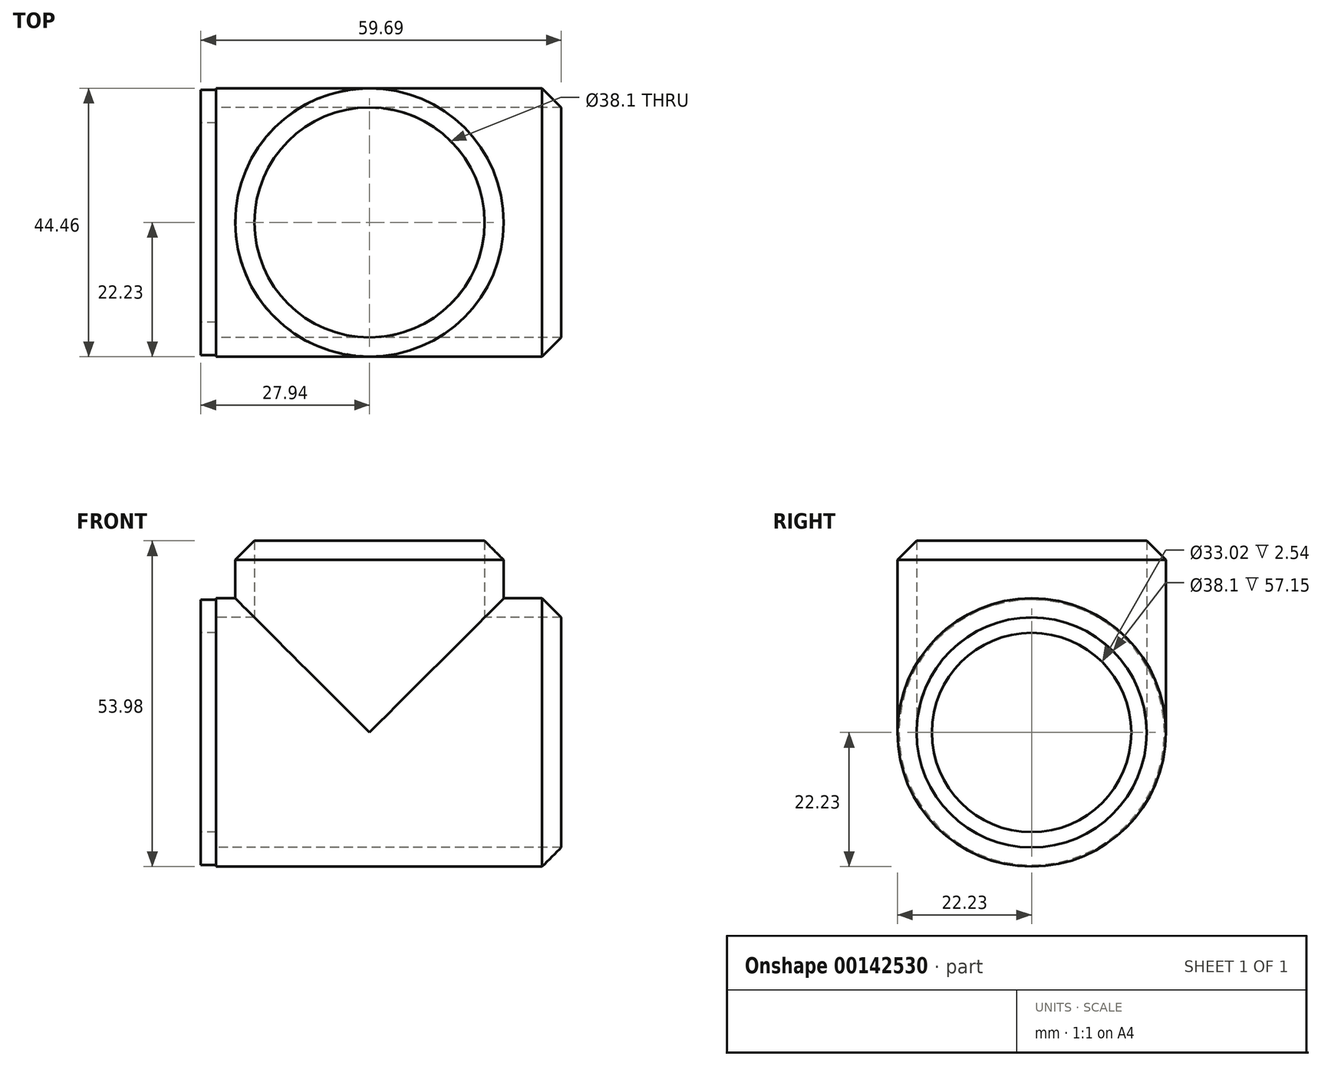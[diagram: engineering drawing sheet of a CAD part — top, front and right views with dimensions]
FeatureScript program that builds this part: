
annotation { "Feature Type Name" : "Feature", "Feature Type Description" : "" }
export const myFeature = defineFeature(function(context is Context, id is Id, definition is map)
    precondition{}
    {
        {
            var Q0;
            Q0=qCreatedBy(makeId("Right.planeOp"),FACE);
            var sketch = newSketch(context, id + "F0", { "sketchPlane" : qUnion([Q0])});
            skCircle(sketch, "E0", {"center": v(0, 0) * mm, "radius": 16.51 * mm});
            skCircle(sketch, "E1", {"center": v(0, 0) * mm, "radius": 18.8 * mm});
            skCircle(sketch, "E2", {"center": v(0, 0) * mm, "radius": 21.97 * mm});
            skSolve(sketch);
        }
        {
            var Q0;
            Q0=makeQuery(id+"F0.imprint","IMPRINT",FACE,{"disambiguationData":[TD([[makeQuery(id+"F0.imprint","IMPRINT",EDGE,{"derivedFrom":sQuery(id+"F0.wireOp",EDGE,"E0")}),-1.0]])]});
            extrude(context, id + "F1", {"entities" : qUnion([Q0]), "depth" : 25.4 * mm});
        }
        {
            var Q0;
            Q0=makeQuery(id+"F0.imprint","IMPRINT",FACE,{"disambiguationData":[TD([[makeQuery(id+"F0.imprint","IMPRINT",EDGE,{"derivedFrom":sQuery(id+"F0.wireOp",EDGE,"E1")}),-1.0]])]});
            var Q1;
            Q1=makeQuery(id+"F0.imprint","IMPRINT",FACE,{"disambiguationData":[TD([[makeQuery(id+"F0.imprint","IMPRINT",EDGE,{"derivedFrom":sQuery(id+"F0.wireOp",EDGE,"E0")}),-1.0]])]});
            extrude(context, id + "F2", {"entities" : qUnion([Q0, Q1]), "operationType" : NewBodyOperationType.ADD, "oppositeDirection" : true, "depth" : 2.54 * mm});
        }
        {
            var Q0;
            Q0=qCreatedBy(makeId("Front.planeOp"),FACE);
            var sketch = newSketch(context, id + "F3", { "sketchPlane" : qUnion([Q0])});
            skLineSegment(sketch, "E3", {"start": v(0, 0) * mm, "end": v(25.4, 0) * mm, "construction": true});
            skLineSegment(sketch, "E4", {"start": v(25.4, 0) * mm, "end": v(25.4, 18.8) * mm, "construction": true});
            skCircle(sketch, "E5", {"center": v(25.4, 18.8) * mm, "radius": 19.05 * mm});
            skCircle(sketch, "E6", {"center": v(25.4, 18.8) * mm, "radius": 22.23 * mm});
            skSolve(sketch);
        }
        {
            var Q0;
            Q0=makeQuery(id+"F3.imprint","IMPRINT",FACE,{"disambiguationData":[TD([[makeQuery(id+"F3.imprint","IMPRINT",EDGE,{"derivedFrom":sQuery(id+"F3.wireOp",EDGE,"E5")}),1.0]])]});
            extrude(context, id + "F4", {"entities" : qUnion([Q0]), "operationType" : NewBodyOperationType.REMOVE, "oppositeDirection" : true, "depth" : 25.4 * mm, "hasSecondDirection" : true, "secondDirectionOppositeDirection" : false, "secondDirectionDepth" : 25.4 * mm});
        }
        {
            var Q0;
            Q0 = qSketchRegion(id + "F3", true);
            extrude(context, id + "F5", {"entities" : qUnion([Q0]), "operationType" : NewBodyOperationType.ADD, "oppositeDirection" : true, "depth" : 25.4 * mm, "hasSecondDirection" : true, "secondDirectionOppositeDirection" : false, "secondDirectionDepth" : 25.4 * mm});
        }
        {
            var Q0;
            Q0=qCreatedBy(makeId("Right.planeOp"),FACE);
            var sketch = newSketch(context, id + "F6", { "sketchPlane" : qUnion([Q0])});
            skCircle(sketch, "E7", {"center": v(0, 0) * mm, "radius": 50.78 * mm});
            skCircle(sketch, "E8", {"center": v(0, 0) * mm, "radius": 18.8 * mm});
            skSolve(sketch);
        }
        {
            var Q0;
            Q0 = qSketchRegion(id + "F6", true);
            extrude(context, id + "F7", {"entities" : qUnion([Q0]), "operationType" : NewBodyOperationType.REMOVE, "depth" : 76.2 * mm});
        }
        {
            var Q0;
            Q0=qCreatedBy(makeId("Top.planeOp"),FACE);
            var sketch = newSketch(context, id + "F8", { "sketchPlane" : qUnion([Q0])});
            skLineSegment(sketch, "E9", {"start": v(0, 0) * mm, "end": v(25.4, 0) * mm, "construction": true});
            skLineSegment(sketch, "E10.bottom", {"start": v(25.4, 0) * mm, "end": v(53.12, 0) * mm});
            skLineSegment(sketch, "E10.top", {"start": v(25.4, 20.3) * mm, "end": v(53.12, 20.3) * mm});
            skLineSegment(sketch, "E10.left", {"start": v(25.4, 0) * mm, "end": v(25.4, 20.3) * mm});
            skLineSegment(sketch, "E10.right", {"start": v(53.12, 0) * mm, "end": v(53.12, 20.3) * mm});
            skLineSegment(sketch, "E11.top", {"start": v(25.4, -23.9) * mm, "end": v(53.12, -23.9) * mm});
            skLineSegment(sketch, "E11.left", {"start": v(25.4, 0) * mm, "end": v(25.4, -23.9) * mm});
            skLineSegment(sketch, "E11.right", {"start": v(53.12, 0) * mm, "end": v(53.12, -23.9) * mm});
            skSolve(sketch);
        }
        {
            var Q0;
            Q0 = qSketchRegion(id + "F8", true);
            extrude(context, id + "F9", {"entities" : qUnion([Q0]), "operationType" : NewBodyOperationType.REMOVE, "depth" : 25.4 * mm, "hasSecondDirection" : true, "secondDirectionOppositeDirection" : true, "secondDirectionDepth" : 25.4 * mm});
        }
        {
            var Q0;
            Q0=qCreatedBy(makeId("Right.planeOp"),FACE);
            var sketch = newSketch(context, id + "F10", { "sketchPlane" : qUnion([Q0])});
            skCircle(sketch, "E12", {"center": v(0, 0) * mm, "radius": 19.05 * mm});
            skCircle(sketch, "E13", {"center": v(0, 0) * mm, "radius": 22.23 * mm});
            skSolve(sketch);
        }
        {
            var Q0;
            Q0 = qSketchRegion(id + "F10", true);
            extrude(context, id + "F11", {"entities" : qUnion([Q0]), "depth" : 57.15 * mm});
        }
        {
            var Q0;
            Q0=qCreatedBy(makeId("Top.planeOp"),FACE);
            var sketch = newSketch(context, id + "F12", { "sketchPlane" : qUnion([Q0])});
            skLineSegment(sketch, "E14", {"start": v(0, 0) * mm, "end": v(25.4, 0) * mm, "construction": true});
            skCircle(sketch, "E15", {"center": v(25.4, 0) * mm, "radius": 19.05 * mm});
            skCircle(sketch, "E16", {"center": v(25.4, 0) * mm, "radius": 22.23 * mm});
            skSolve(sketch);
        }
        {
            var Q0;
            Q0 = qSketchRegion(id + "F12", true);
            extrude(context, id + "F13", {"entities" : qUnion([Q0]), "operationType" : NewBodyOperationType.ADD, "depth" : 31.75 * mm});
        }
        {
            var Q0;
            Q0=makeQuery(id+"F12.imprint","IMPRINT",FACE,{"disambiguationData":[TD([[makeQuery(id+"F12.imprint","IMPRINT",EDGE,{"derivedFrom":sQuery(id+"F12.wireOp",EDGE,"E15")}),1.0]])]});
            extrude(context, id + "F14", {"entities" : qUnion([Q0]), "operationType" : NewBodyOperationType.REMOVE, "depth" : 25.4 * mm});
        }
        {
            var Q0;
            Q0=makeQuery(id+"F10.imprint","IMPRINT",FACE,{"disambiguationData":[TD([[makeQuery(id+"F10.imprint","IMPRINT",EDGE,{"derivedFrom":sQuery(id+"F10.wireOp",EDGE,"E12")}),1.0]])]});
            extrude(context, id + "F15", {"entities" : qUnion([Q0]), "operationType" : NewBodyOperationType.REMOVE, "depth" : 82.55 * mm});
        }
        {
            var Q0;
            Q0=qCreatedBy(makeId("Front.planeOp"),FACE);
            var sketch = newSketch(context, id + "F16", { "sketchPlane" : qUnion([Q0])});
            skLineSegment(sketch, "E17", {"start": v(0, 0) * mm, "end": v(25.4, 0) * mm, "construction": true});
            skLineSegment(sketch, "E18", {"start": v(25.4, 0) * mm, "end": v(25.4, 31.75) * mm, "construction": true});
            skLineSegment(sketch, "E19", {"start": v(25.4, 31.75) * mm, "end": v(3.17, 31.75) * mm, "construction": true});
            skLineSegment(sketch, "E20", {"start": v(3.18, 31.75) * mm, "end": v(3.18, 28.57) * mm});
            skLineSegment(sketch, "E21", {"start": v(3.18, 28.57) * mm, "end": v(6.35, 31.75) * mm});
            skLineSegment(sketch, "E22", {"start": v(6.35, 31.75) * mm, "end": v(3.18, 31.75) * mm});
            skSolve(sketch);
        }
        {
            var Q0;
            Q0 = qSketchRegion(id + "F16", true);
            var Q1;
            Q1=sQuery(id+"F16.wireOp",EDGE,"E18");
            revolve(context, id + "F17", {"operationType" : NewBodyOperationType.REMOVE, "entities" : qUnion([Q0]), "axis" : qUnion([Q1]), "revolveType" : RevolveType.FULL, "oppositeDirection" : true});
        }
        {
            var Q0;
            Q0=qCreatedBy(makeId("Front.planeOp"),FACE);
            var sketch = newSketch(context, id + "F18", { "sketchPlane" : qUnion([Q0])});
            skLineSegment(sketch, "E23", {"start": v(0, 0) * mm, "end": v(57.15, 0) * mm, "construction": true});
            skLineSegment(sketch, "E24", {"start": v(57.15, 0) * mm, "end": v(57.15, 22.22) * mm, "construction": true});
            skLineSegment(sketch, "E25", {"start": v(57.15, 22.23) * mm, "end": v(53.98, 22.23) * mm});
            skLineSegment(sketch, "E26", {"start": v(53.98, 22.22) * mm, "end": v(57.15, 19.05) * mm});
            skLineSegment(sketch, "E27", {"start": v(57.15, 19.05) * mm, "end": v(57.15, 22.22) * mm});
            skSolve(sketch);
        }
        {
            var Q0;
            Q0 = qSketchRegion(id + "F18", true);
            var Q1;
            Q1=sQuery(id+"F18.wireOp",EDGE,"E23");
            revolve(context, id + "F19", {"operationType" : NewBodyOperationType.REMOVE, "entities" : qUnion([Q0]), "axis" : qUnion([Q1]), "revolveType" : RevolveType.FULL, "oppositeDirection" : true});
        }
    });
